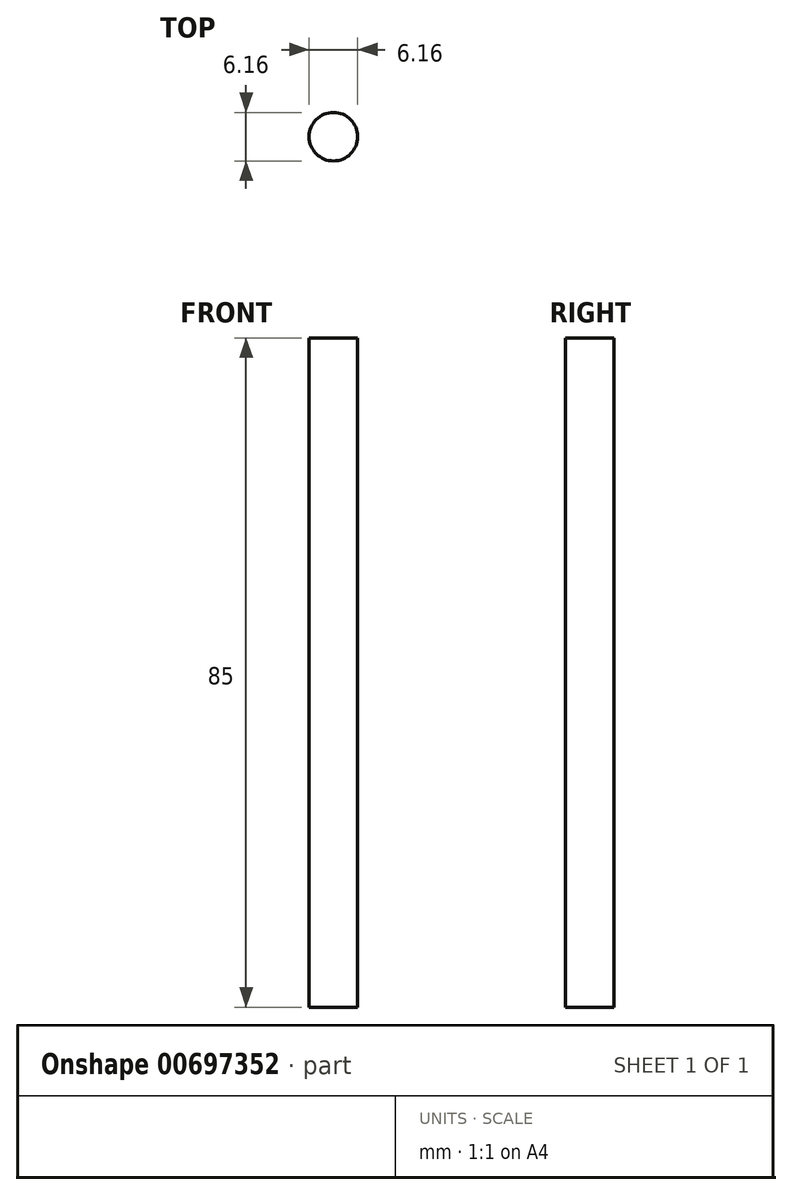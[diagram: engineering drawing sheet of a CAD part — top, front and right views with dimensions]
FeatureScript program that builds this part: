
annotation { "Feature Type Name" : "Feature", "Feature Type Description" : "" }
export const myFeature = defineFeature(function(context is Context, id is Id, definition is map)
    precondition{}
    {
        {
            var Q0;
            Q0=qCreatedBy(makeId("Top.planeOp"),FACE);
            var sketch = newSketch(context, id + "F0", { "sketchPlane" : qUnion([Q0])});
            skCircle(sketch, "E0", {"center": v(0, 0) * mm, "radius": 3.08 * mm});
            skSolve(sketch);
        }
        {
            var Q0;
            Q0 = qSketchRegion(id + "F0", true);
            extrude(context, id + "F1", {"entities" : qUnion([Q0]), "depth" : 85 * mm, "offsetDistance" : 25 * mm});
        }
    });
